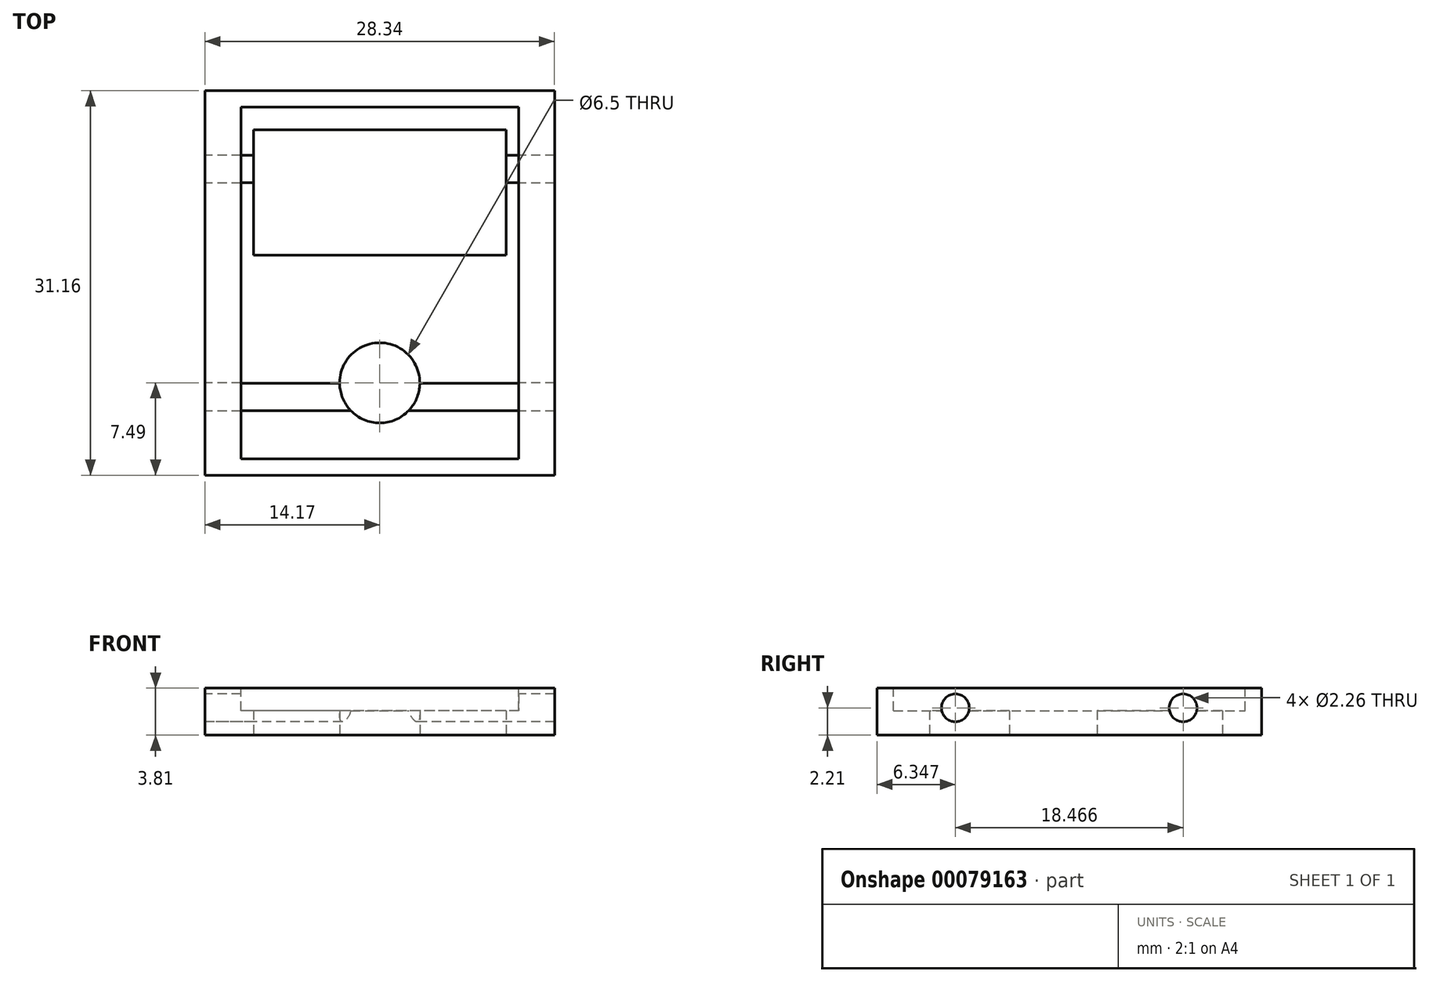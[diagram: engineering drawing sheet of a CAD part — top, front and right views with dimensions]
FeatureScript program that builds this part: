
annotation { "Feature Type Name" : "Feature", "Feature Type Description" : "" }
export const myFeature = defineFeature(function(context is Context, id is Id, definition is map)
    precondition{}
    {
        {
            var Q0;
            Q0=qCreatedBy(makeId("Top.planeOp"),FACE);
            var sketch = newSketch(context, id + "F0", { "sketchPlane" : qUnion([Q0])});
            skLineSegment(sketch, "E0.bottom", {"start": v(14.17, -15.58) * mm, "end": v(-14.17, -15.58) * mm});
            skLineSegment(sketch, "E0.top", {"start": v(14.17, 15.58) * mm, "end": v(-14.17, 15.58) * mm});
            skLineSegment(sketch, "E0.left", {"start": v(14.17, -15.58) * mm, "end": v(14.17, 15.58) * mm});
            skLineSegment(sketch, "E0.right", {"start": v(-14.17, -15.58) * mm, "end": v(-14.17, 15.58) * mm});
            skPoint(sketch, "E0.middle", {"position": v(0, 0) * mm});
            skSolve(sketch);
        }
        {
            var Q0;
            Q0 = qSketchRegion(id + "F0", true);
            extrude(context, id + "F1", {"entities" : qUnion([Q0]), "depth" : 3.8 * mm});
        }
        {
            var Q0;
            Q0=makeQuery(id+"F1.opExtrude","CAP_FACE",FACE,{"disambiguationData":[OSD([sQuery(id+"F0.wireOp",EDGE,"E0.bottom"),sQuery(id+"F0.wireOp",EDGE,"E0.top"),sQuery(id+"F0.wireOp",EDGE,"E0.left"),sQuery(id+"F0.wireOp",EDGE,"E0.right")])],"isStart":false});
            var sketch = newSketch(context, id + "F2", { "sketchPlane" : qUnion([Q0])});
            skLineSegment(sketch, "E1.bottom", {"start": v(11.25, -14.25) * mm, "end": v(-11.25, -14.25) * mm});
            skLineSegment(sketch, "E1.top", {"start": v(11.25, 14.25) * mm, "end": v(-11.25, 14.25) * mm});
            skLineSegment(sketch, "E1.left", {"start": v(11.25, -14.25) * mm, "end": v(11.25, 14.25) * mm});
            skLineSegment(sketch, "E1.right", {"start": v(-11.25, -14.25) * mm, "end": v(-11.25, 14.25) * mm});
            skPoint(sketch, "E1.middle", {"position": v(0, 0) * mm});
            skSolve(sketch);
        }
        {
            var Q0;
            Q0 = qSketchRegion(id + "F2", true);
            extrude(context, id + "F3", {"entities" : qUnion([Q0]), "operationType" : NewBodyOperationType.REMOVE, "oppositeDirection" : true, "depth" : 1.83 * mm});
        }
        {
            var Q0;
            Q0=makeQuery(id+"F1.opExtrude","SWEPT_FACE",FACE,{"disambiguationData":[OSD([sQuery(id+"F0.wireOp",EDGE,"E0.right")])]});
            var sketch = newSketch(context, id + "F4", { "sketchPlane" : qUnion([Q0])});
            skCircle(sketch, "E2", {"center": v(9.23, 2.2) * mm, "radius": 1.13 * mm});
            skCircle(sketch, "E3", {"center": v(-9.23, 2.2) * mm, "radius": 1.13 * mm});
            skSolve(sketch);
        }
        {
            var Q0;
            Q0 = qSketchRegion(id + "F4", true);
            extrude(context, id + "F5", {"entities" : qUnion([Q0]), "operationType" : NewBodyOperationType.REMOVE, "endBound" : BoundingType.THROUGH_ALL, "oppositeDirection" : true, "depth" : 25.4 * mm});
        }
        {
            var Q0;
            Q0=makeQuery(id+"F1.opExtrude","CAP_FACE",FACE,{"disambiguationData":[OSD([sQuery(id+"F0.wireOp",EDGE,"E0.bottom"),sQuery(id+"F0.wireOp",EDGE,"E0.top"),sQuery(id+"F0.wireOp",EDGE,"E0.left"),sQuery(id+"F0.wireOp",EDGE,"E0.right")])],"isStart":true});
            var sketch = newSketch(context, id + "F6", { "sketchPlane" : qUnion([Q0])});
            skCircle(sketch, "E4", {"center": v(0, 8.09) * mm, "radius": 3.25 * mm});
            skLineSegment(sketch, "E5.bottom", {"start": v(-10.24, -2.25) * mm, "end": v(10.24, -2.25) * mm});
            skLineSegment(sketch, "E5.top", {"start": v(-10.24, -12.4) * mm, "end": v(10.24, -12.4) * mm});
            skLineSegment(sketch, "E5.left", {"start": v(-10.24, -2.25) * mm, "end": v(-10.24, -12.4) * mm});
            skLineSegment(sketch, "E5.right", {"start": v(10.24, -2.25) * mm, "end": v(10.24, -12.4) * mm});
            skSolve(sketch);
        }
        {
            var Q0;
            Q0 = qSketchRegion(id + "F6", true);
            extrude(context, id + "F7", {"entities" : qUnion([Q0]), "operationType" : NewBodyOperationType.REMOVE, "endBound" : BoundingType.THROUGH_ALL, "oppositeDirection" : true, "depth" : 25.4 * mm});
        }
    });
